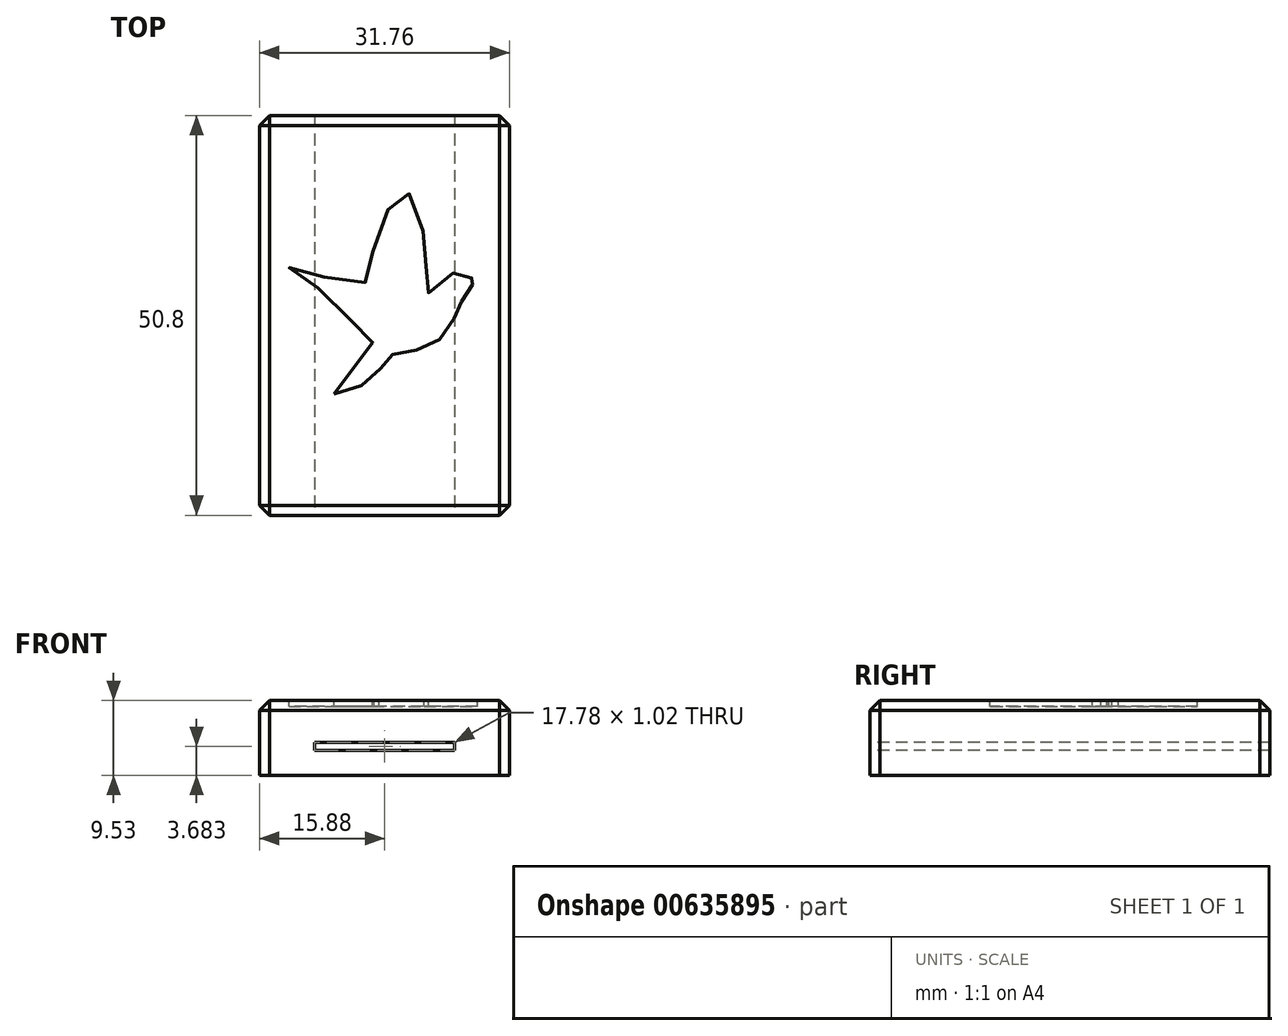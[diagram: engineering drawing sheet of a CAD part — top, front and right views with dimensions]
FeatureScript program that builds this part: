
annotation { "Feature Type Name" : "Feature", "Feature Type Description" : "" }
export const myFeature = defineFeature(function(context is Context, id is Id, definition is map)
    precondition{}
    {
        {
            var Q0;
            Q0=qCreatedBy(makeId("Top.planeOp"),FACE);
            var sketch = newSketch(context, id + "F0", { "sketchPlane" : qUnion([Q0])});
            skLineSegment(sketch, "E0.bottom", {"start": v(15.88, -25.4) * mm, "end": v(-15.88, -25.4) * mm});
            skLineSegment(sketch, "E0.top", {"start": v(15.88, 25.4) * mm, "end": v(-15.88, 25.4) * mm});
            skLineSegment(sketch, "E0.left", {"start": v(15.88, -25.4) * mm, "end": v(15.88, 25.4) * mm});
            skLineSegment(sketch, "E0.right", {"start": v(-15.88, -25.4) * mm, "end": v(-15.88, 25.4) * mm});
            skPoint(sketch, "E0.middle", {"position": v(0, 0) * mm});
            skSolve(sketch);
        }
        {
            var Q0;
            Q0=makeQuery(id+"F0.imprint","IMPRINT",FACE,{"disambiguationData":[TD([[makeQuery(id+"F0.imprint","IMPRINT",EDGE,{"derivedFrom":sQuery(id+"F0.wireOp",EDGE,"E0.bottom")}),-1.0]])]});
            extrude(context, id + "F1", {"entities" : qUnion([Q0]), "depth" : 9.52 * mm, "offsetDistance" : 25.4 * mm});
        }
        {
            var Q0;
            Q0=makeQuery(id+"F1.opExtrude","SWEPT_FACE",FACE,{"disambiguationData":[OSD([sQuery(id+"F0.wireOp",EDGE,"E0.bottom")])]});
            var sketch = newSketch(context, id + "F2", { "sketchPlane" : qUnion([Q0])});
            skLineSegment(sketch, "E1.bottom", {"start": v(8.9, 3.18) * mm, "end": v(-8.9, 3.18) * mm});
            skLineSegment(sketch, "E1.top", {"start": v(8.9, 4.2) * mm, "end": v(-8.89, 4.2) * mm});
            skLineSegment(sketch, "E1.left", {"start": v(8.9, 3.18) * mm, "end": v(8.9, 4.2) * mm});
            skLineSegment(sketch, "E1.right", {"start": v(-8.9, 3.18) * mm, "end": v(-8.9, 4.2) * mm});
            skPoint(sketch, "E1.middle", {"position": v(0, 3.68) * mm});
            skSolve(sketch);
        }
        {
            var Q0;
            Q0=makeQuery(id+"F2.imprint","IMPRINT",FACE,{"disambiguationData":[TD([[makeQuery(id+"F2.imprint","IMPRINT",EDGE,{"derivedFrom":sQuery(id+"F2.wireOp",EDGE,"E1.bottom")}),-1.0]])]});
            extrude(context, id + "F3", {"entities" : qUnion([Q0]), "operationType" : NewBodyOperationType.REMOVE, "oppositeDirection" : true, "depth" : 58.42 * mm, "offsetDistance" : 25.4 * mm});
        }
        {
            var Q0;
            Q0=makeQuery(id+"F1.opExtrude","CAP_EDGE",EDGE,{"disambiguationData":[OSD([sQuery(id+"F0.wireOp",EDGE,"E0.right")])],"isStart":false});
            var Q1;
            Q1=makeQuery(id+"F1.opExtrude","CAP_EDGE",EDGE,{"disambiguationData":[OSD([sQuery(id+"F0.wireOp",EDGE,"E0.left")])],"isStart":false});
            var Q2;
            Q2=makeQuery(id+"F1.opExtrude","CAP_EDGE",EDGE,{"disambiguationData":[OSD([sQuery(id+"F0.wireOp",EDGE,"E0.bottom")])],"isStart":false});
            var Q3;
            Q3=makeQuery(id+"F1.opExtrude","CAP_EDGE",EDGE,{"disambiguationData":[OSD([sQuery(id+"F0.wireOp",EDGE,"E0.top")])],"isStart":false});
            var Q4;
            Q4=makeQuery(id+"F1.opExtrude","SWEPT_EDGE",EDGE,{"disambiguationData":[OSD([sQuery(id+"F0.wireOp",EDGE,"E0.bottom"),sQuery(id+"F0.wireOp",EDGE,"E0.right")])]});
            var Q5;
            Q5=makeQuery(id+"F1.opExtrude","SWEPT_EDGE",EDGE,{"disambiguationData":[OSD([sQuery(id+"F0.wireOp",EDGE,"E0.top"),sQuery(id+"F0.wireOp",EDGE,"E0.right")])]});
            var Q6;
            Q6=makeQuery(id+"F1.opExtrude","SWEPT_EDGE",EDGE,{"disambiguationData":[OSD([sQuery(id+"F0.wireOp",EDGE,"E0.top"),sQuery(id+"F0.wireOp",EDGE,"E0.left")])]});
            var Q7;
            Q7=makeQuery(id+"F1.opExtrude","SWEPT_EDGE",EDGE,{"disambiguationData":[OSD([sQuery(id+"F0.wireOp",EDGE,"E0.bottom"),sQuery(id+"F0.wireOp",EDGE,"E0.left")])]});
            chamfer(context, id + "F4", {"entities" : qUnion([Q0, Q1, Q2, Q3, Q4, Q5, Q6, Q7]), "width" : 1.27 * mm, "tangentPropagation" : true});
        }
        {
            var Q0;
            Q0=makeQuery(id+"F1.opExtrude","CAP_FACE",FACE,{"disambiguationData":[OSD([sQuery(id+"F0.wireOp",EDGE,"E0.bottom"),sQuery(id+"F0.wireOp",EDGE,"E0.top"),sQuery(id+"F0.wireOp",EDGE,"E0.left"),sQuery(id+"F0.wireOp",EDGE,"E0.right")])],"isStart":false});
            var sketch = newSketch(context, id + "F5", { "sketchPlane" : qUnion([Q0])});
            skSolve(sketch);
        }
        {
            var Q0;
            {var subQ0=sQuery(id+"F0.wireOp",EDGE,"E0.right");var subQ1=sQuery(id+"F0.wireOp",EDGE,"E0.left");var subQ2=sQuery(id+"F0.wireOp",EDGE,"E0.top");var subQ3=sQuery(id+"F0.wireOp",EDGE,"E0.bottom");var subQ4=makeQuery(id+"F1.opExtrude","CAP_FACE",FACE,{"disambiguationData":[OSD([subQ3,subQ2,subQ1,subQ0])],"isStart":false});Q0=makeQuery(id+"F5.imprint","IMPRINT",FACE,{"disambiguationData":[TD([[makeQuery(id+"F5.imprint","IMPRINT",EDGE,{"derivedFrom":makeQuery(id+"F4.opChamfer","BLEND_EDGE",EDGE,{"blendedFrom":[makeQuery(id+"F1.opExtrude","CAP_EDGE",EDGE,{"disambiguationData":[OSD([subQ3])],"isStart":false}),subQ4],"blendedInto":[subQ4]})}),1.0]])]});}
            var sketch = newSketch(context, id + "F6", { "sketchPlane" : qUnion([Q0])});
            skFitSpline(sketch, "E2", {"points": [v(-6.44, -10) * mm, v(-3.32, -5.74) * mm, v(-1.29, -3.2) * mm, v(-0.75, -2.55) * mm, v(-2.87, -1.7) * mm, v(-4.6, -0.26) * mm, v(-6.65, 1.42) * mm, v(-8.03, 3.05) * mm, v(-9.47, 4.34) * mm, v(-10.38, 4.97) * mm, v(-11.8, 5.61) * mm, v(-12.12, 6.17) * mm, v(-10.46, 5.52) * mm, v(-8.82, 5.18) * mm, v(-7.5, 4.84) * mm, v(-5.83, 5) * mm, v(-4.01, 4.63) * mm, v(-1.88, 4.04) * mm, v(-1.39, 4.02) * mm, v(-1.5, 6.34) * mm, v(-1.42, 8.8) * mm, v(-0.99, 10.68) * mm, v(0, 12.8) * mm, v(1.33, 14.66) * mm, v(2.33, 15.93) * mm, v(2.57, 16.24) * mm, v(3.16, 15.36) * mm, v(3.87, 13.77) * mm, v(4.48, 12.24) * mm, v(4.9, 10.57) * mm, v(5.33, 9.4) * mm, v(5.54, 7.59) * mm, v(5.3, 6.46) * mm, v(5, 5.31) * mm, v(5.03, 4.35) * mm, v(5.13, 3.48) * mm, v(5.48, 2.85) * mm, v(6, 3.57) * mm, v(7.14, 4.64) * mm, v(8.1, 5.25) * mm, v(8.74, 5.36) * mm, v(9.3, 5.34) * mm, v(9.77, 5.17) * mm, v(10.22, 5) * mm, v(10.52, 4.81) * mm, v(10.7, 4.74) * mm, v(11.06, 4.78) * mm, v(11.24, 4.87) * mm, v(11.45, 4.9) * mm, v(11.65, 4.86) * mm, v(11.76, 4.77) * mm, v(11.74, 4.64) * mm, v(11.6, 4.48) * mm, v(11.49, 4.36) * mm, v(11.33, 4.16) * mm, v(11.02, 3.67) * mm, v(10.84, 3.34) * mm, v(10.65, 2.95) * mm, v(10.46, 2.65) * mm, v(10.23, 2.27) * mm, v(9.86, 1.86) * mm, v(9.62, 1.63) * mm, v(9.46, 1.46) * mm, v(9.32, 1.33) * mm, v(9.22, 0.93) * mm, v(9.09, 0.34) * mm, v(8.95, -0.13) * mm, v(8.74, -0.65) * mm, v(8.5, -1.2) * mm, v(8.26, -1.65) * mm, v(7.76, -2.32) * mm, v(7.03, -2.99) * mm, v(6.27, -3.42) * mm, v(5.46, -3.88) * mm, v(4.95, -4.02) * mm, v(4.6, -4.1) * mm, v(3.95, -4.45) * mm, v(3.41, -4.55) * mm, v(2.77, -4.66) * mm, v(2.08, -4.79) * mm, v(1.45, -4.9) * mm, v(0.83, -5) * mm, v(0.43, -5.08) * mm, v(-0.13, -5.42) * mm, v(-0.39, -5.8) * mm, v(-0.5, -6.26) * mm, v(-0.54, -6.64) * mm, v(-0.55, -6.92) * mm, v(-0.66, -7.26) * mm, v(-1.17, -7.62) * mm, v(-1.84, -8.15) * mm, v(-2.96, -8.94) * mm, v(-3.97, -9.45) * mm, v(-4.95, -9.86) * mm, v(-5.85, -10.06) * mm, v(-6.44, -10) * mm]});
            skSolve(sketch);
        }
        {
            var Q0;
            Q0=makeQuery(id+"F6.imprint","IMPRINT",FACE,{"disambiguationData":[TD([[makeQuery(id+"F6.imprint","IMPRINT",EDGE,{"derivedFrom":sQuery(id+"F6.wireOp",EDGE,"E2")}),-1.0]])]});
            var Q1;
            Q1=sQuery(id+"F6.wireOp",EDGE,"E2");
            extrude(context, id + "F7", {"entities" : qUnion([Q0]), "operationType" : NewBodyOperationType.REMOVE, "surfaceEntities" : qUnion([Q1]), "oppositeDirection" : true, "depth" : 0.79 * mm, "offsetDistance" : 25.4 * mm});
        }
    });
